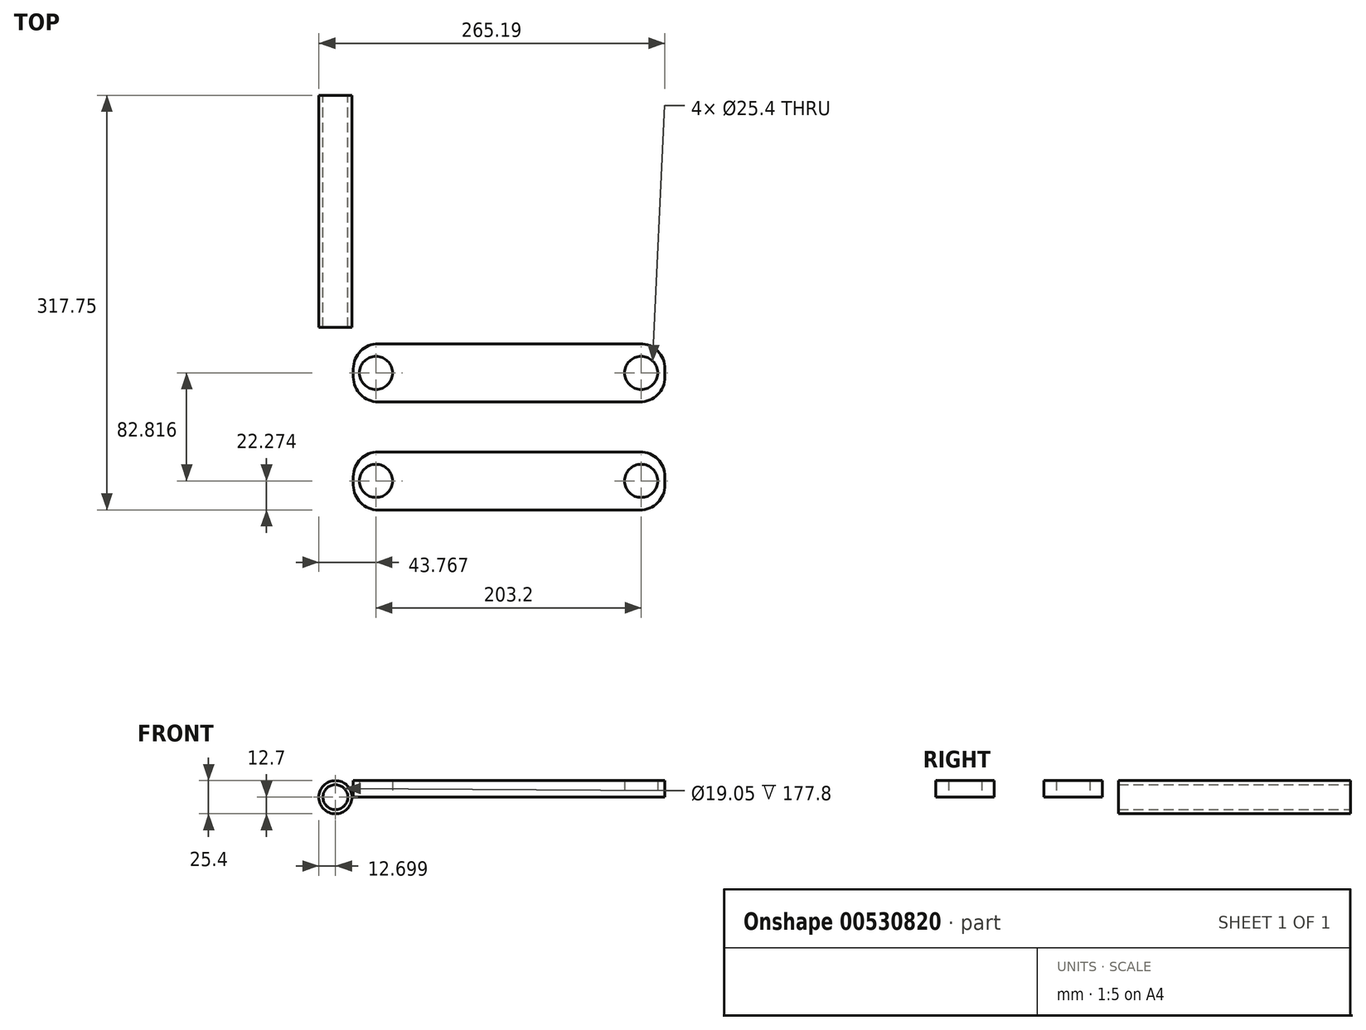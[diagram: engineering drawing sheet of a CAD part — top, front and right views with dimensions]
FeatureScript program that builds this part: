
annotation { "Feature Type Name" : "Feature", "Feature Type Description" : "" }
export const myFeature = defineFeature(function(context is Context, id is Id, definition is map)
    precondition{}
    {
        {
            var Q0;
            Q0=qCreatedBy(makeId("Top.planeOp"),FACE);
            var sketch = newSketch(context, id + "F0", { "sketchPlane" : qUnion([Q0])});
            skLineSegment(sketch, "E0.bottom", {"start": v(-100.32, -22.27) * mm, "end": v(100.32, -22.27) * mm});
            skLineSegment(sketch, "E0.top", {"start": v(-100.32, 22.27) * mm, "end": v(100.32, 22.27) * mm});
            skLineSegment(sketch, "E0.left", {"start": v(-119.37, -3.22) * mm, "end": v(-119.37, 3.22) * mm});
            skLineSegment(sketch, "E0.right", {"start": v(119.37, -3.22) * mm, "end": v(119.37, 3.22) * mm});
            skPoint(sketch, "E0.middle", {"position": v(0, 0) * mm});
            skCircle(sketch, "E1", {"center": v(-102.05, 0) * mm, "radius": 12.7 * mm});
            skCircle(sketch, "E2", {"center": v(101.15, 0) * mm, "radius": 12.7 * mm});
            skPoint(sketch, "E3.visualSharp", {"position": v(-119.37, 22.27) * mm});
            skArc(sketch, "E3.filletArc", {"start": v(-100.32, 22.27) * mm, "mid": v(-113.79, 16.7) * mm, "end": v(-119.37, 3.22) * mm});
            skPoint(sketch, "E4.visualSharp", {"position": v(-119.37, -22.27) * mm});
            skArc(sketch, "E4.filletArc", {"start": v(-119.37, -3.22) * mm, "mid": v(-113.79, -16.7) * mm, "end": v(-100.32, -22.27) * mm});
            skPoint(sketch, "E5.visualSharp", {"position": v(119.37, -22.27) * mm});
            skArc(sketch, "E5.filletArc", {"start": v(100.32, -22.27) * mm, "mid": v(113.79, -16.7) * mm, "end": v(119.37, -3.22) * mm});
            skPoint(sketch, "E6.visualSharp", {"position": v(119.37, 22.27) * mm});
            skArc(sketch, "E6.filletArc", {"start": v(119.37, 3.22) * mm, "mid": v(113.79, 16.7) * mm, "end": v(100.32, 22.27) * mm});
            skLineSegment(sketch, "E7", {"start": v(0, 47.12) * mm, "end": v(0, -41.4) * mm, "construction": true});
            skLineSegment(sketch, "E8", {"start": v(-127.63, -41.4) * mm, "end": v(126.18, -41.4) * mm, "construction": true});
            skLineSegment(sketch, "E9.MirrorCS", {"start": v(119.37, -79.6) * mm, "end": v(119.37, -86.04) * mm});
            skLineSegment(sketch, "E10.MirrorCS", {"start": v(-119.37, -79.6) * mm, "end": v(-119.37, -86.04) * mm});
            skPoint(sketch, "E11.MirrorP", {"position": v(-119.37, -105.1) * mm});
            skPoint(sketch, "E12.MirrorP", {"position": v(119.37, -60.54) * mm});
            skArc(sketch, "E13.MirrorCS", {"start": v(-100.32, -105.1) * mm, "mid": v(-113.79, -99.51) * mm, "end": v(-119.37, -86.04) * mm});
            skLineSegment(sketch, "E14.MirrorCS", {"start": v(-100.32, -105.1) * mm, "end": v(100.32, -105.1) * mm});
            skArc(sketch, "E15.MirrorCS", {"start": v(-119.37, -79.6) * mm, "mid": v(-113.79, -66.12) * mm, "end": v(-100.32, -60.54) * mm});
            skPoint(sketch, "E16.MirrorP", {"position": v(0, -82.82) * mm});
            skCircle(sketch, "E17.MirrorC", {"center": v(-102.05, -82.82) * mm, "radius": 12.7 * mm});
            skPoint(sketch, "E18.MirrorP", {"position": v(119.37, -105.1) * mm});
            skPoint(sketch, "E19.MirrorP", {"position": v(-119.37, -60.54) * mm});
            skCircle(sketch, "E20.MirrorC", {"center": v(101.15, -82.82) * mm, "radius": 12.7 * mm});
            skArc(sketch, "E21.MirrorCS", {"start": v(100.32, -60.54) * mm, "mid": v(113.79, -66.12) * mm, "end": v(119.37, -79.6) * mm});
            skLineSegment(sketch, "E22.MirrorCS", {"start": v(-100.32, -60.54) * mm, "end": v(100.32, -60.54) * mm});
            skLineSegment(sketch, "E23.MirrorCS", {"start": v(0, -129.94) * mm, "end": v(0, -41.4) * mm, "construction": true});
            skArc(sketch, "E24.MirrorCS", {"start": v(119.37, -86.04) * mm, "mid": v(113.79, -99.51) * mm, "end": v(100.32, -105.1) * mm});
            skSolve(sketch);
        }
        {
            var Q0;
            Q0=makeQuery(id+"F0.imprint","IMPRINT",FACE,{"disambiguationData":[TD([[makeQuery(id+"F0.imprint","IMPRINT",EDGE,{"derivedFrom":sQuery(id+"F0.wireOp",EDGE,"E0.bottom")}),1.0]])]});
            var Q1;
            Q1=makeQuery(id+"F0.imprint","IMPRINT",FACE,{"disambiguationData":[TD([[makeQuery(id+"F0.imprint","IMPRINT",EDGE,{"derivedFrom":sQuery(id+"F0.wireOp",EDGE,"E9.MirrorCS")}),-1.0]])]});
            extrude(context, id + "F1", {"entities" : qUnion([Q0, Q1]), "depth" : 12.7 * mm, "offsetDistance" : 25.4 * mm});
        }
        {
            var Q0;
            Q0=qCreatedBy(makeId("Top.planeOp"),FACE);
            var sketch = newSketch(context, id + "F2", { "sketchPlane" : qUnion([Q0])});
            skLineSegment(sketch, "E25", {"start": v(-133.12, 212.66) * mm, "end": v(-133.12, 34.86) * mm, "construction": true});
            skLineSegment(sketch, "E26", {"start": v(-120.42, 34.86) * mm, "end": v(-120.42, 212.66) * mm});
            skLineSegment(sketch, "E27.0", {"start": v(-123.6, 34.86) * mm, "end": v(-123.6, 212.66) * mm});
            skLineSegment(sketch, "E28", {"start": v(-120.42, 212.66) * mm, "end": v(-123.6, 212.66) * mm});
            skLineSegment(sketch, "E29", {"start": v(-120.42, 34.86) * mm, "end": v(-123.6, 34.86) * mm});
            skSolve(sketch);
        }
        {
            var Q0;
            Q0=makeQuery(id+"F2.imprint","IMPRINT",FACE,{"disambiguationData":[TD([[makeQuery(id+"F2.imprint","IMPRINT",EDGE,{"derivedFrom":sQuery(id+"F2.wireOp",EDGE,"E26")}),1.0]])]});
            var Q1;
            Q1=sQuery(id+"F2.wireOp",EDGE,"E25");
            revolve(context, id + "F3", {"entities" : qUnion([Q0]), "axis" : qUnion([Q1]), "revolveType" : RevolveType.FULL});
        }
    });
